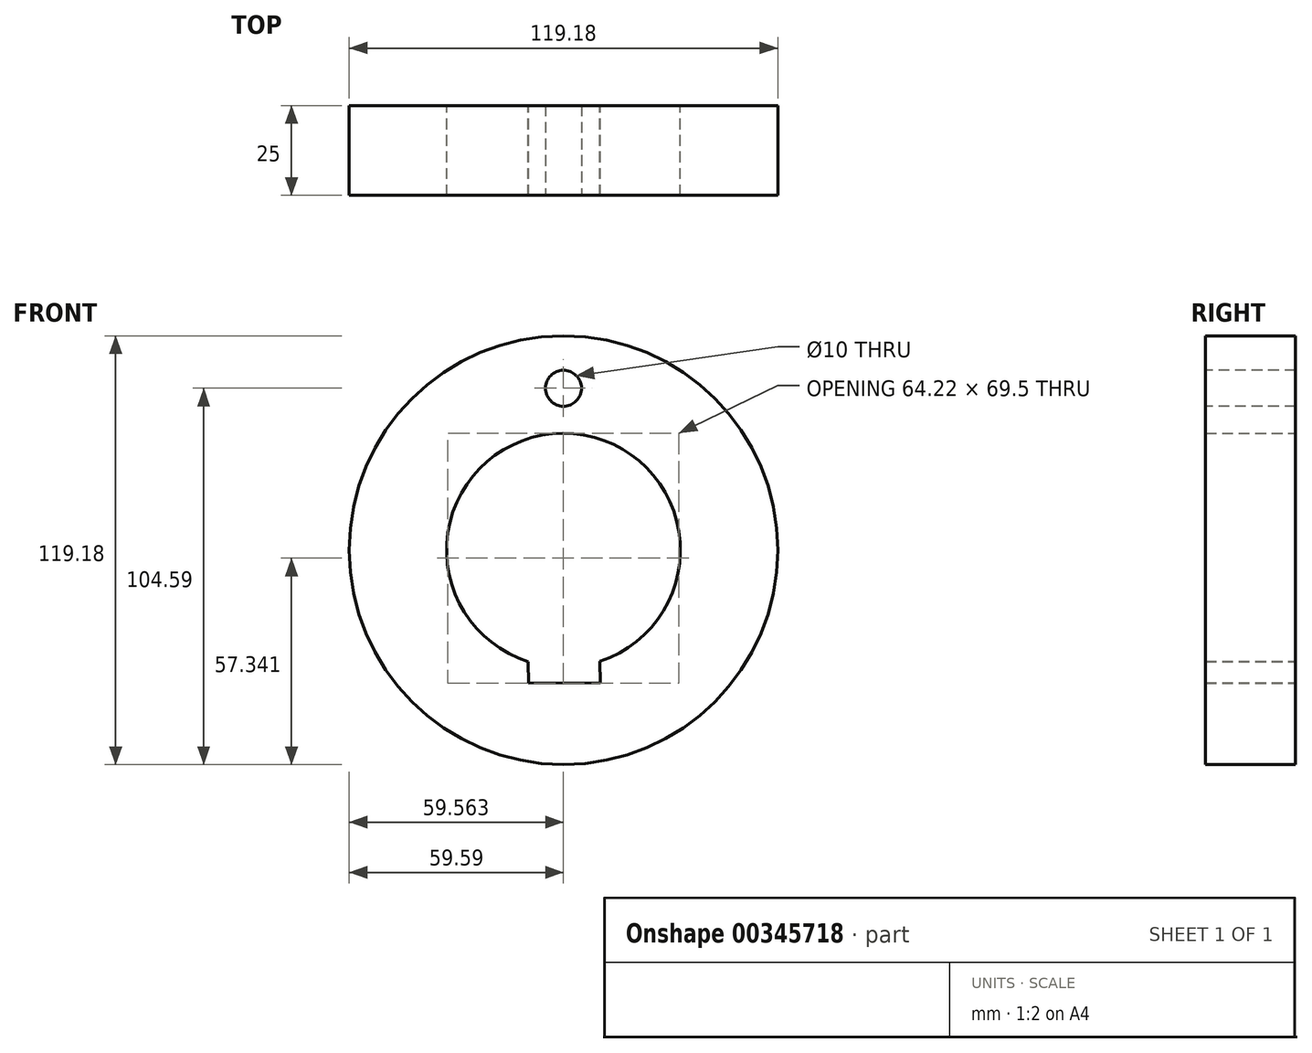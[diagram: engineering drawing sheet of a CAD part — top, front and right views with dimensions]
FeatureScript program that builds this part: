
annotation { "Feature Type Name" : "Feature", "Feature Type Description" : "" }
export const myFeature = defineFeature(function(context is Context, id is Id, definition is map)
    precondition{}
    {
        {
            var Q0;
            Q0=qCreatedBy(makeId("Front.planeOp"),FACE);
            var sketch = newSketch(context, id + "F0", { "sketchPlane" : qUnion([Q0])});
            skPoint(sketch, "E0.middle", {"position": v(0, -32.25) * mm});
            skLineSegment(sketch, "E1", {"start": v(-9.77, -31) * mm, "end": v(-9.73, -37) * mm});
            skLineSegment(sketch, "E2", {"start": v(-9.73, -37) * mm, "end": v(10.26, -36.89) * mm});
            skLineSegment(sketch, "E3", {"start": v(10.26, -36.89) * mm, "end": v(10.1, -30.9) * mm});
            skArc(sketch, "E4", {"start": v(10.1, -30.9) * mm, "mid": v(-0.17, 32.5) * mm, "end": v(-9.77, -31) * mm});
            skCircle(sketch, "E5", {"center": v(0, 0) * mm, "radius": 59.59 * mm});
            skCircle(sketch, "E6", {"center": v(0, 45) * mm, "radius": 5 * mm});
            skSolve(sketch);
        }
        {
            var Q0;
            Q0=makeQuery(id+"F0.imprint","IMPRINT",FACE,{"disambiguationData":[TD([[makeQuery(id+"F0.imprint","IMPRINT",EDGE,{"derivedFrom":sQuery(id+"F0.wireOp",EDGE,"E6")}),1.0]])]});
            var Q1;
            Q1=makeQuery(id+"F0.imprint","IMPRINT",FACE,{"disambiguationData":[TD([[makeQuery(id+"F0.imprint","IMPRINT",EDGE,{"derivedFrom":sQuery(id+"F0.wireOp",EDGE,"E1")}),-1.0]])]});
            extrude(context, id + "F1", {"entities" : qUnion([Q0, Q1]), "depth" : 25 * mm});
        }
        {
            var Q0;
            Q0=makeQuery(id+"F1.opExtrude","CAP_FACE",FACE,{"disambiguationData":[OSD([sQuery(id+"F0.wireOp",EDGE,"E1"),sQuery(id+"F0.wireOp",EDGE,"E2"),sQuery(id+"F0.wireOp",EDGE,"E3"),sQuery(id+"F0.wireOp",EDGE,"E4"),sQuery(id+"F0.wireOp",EDGE,"E5")])],"isStart":false});
            var sketch = newSketch(context, id + "F2", { "sketchPlane" : qUnion([Q0])});
            skCircle(sketch, "E7", {"center": v(0, 45) * mm, "radius": 5 * mm});
            skSolve(sketch);
        }
        {
            var Q0;
            Q0=sQuery(id+"F2.wireOp",VERTEX,"E7.center");
            var Q1;
            Q1=makeQuery(id+"F1.opExtrude","SWEPT_BODY",BODY,{"disambiguationData":[OSD([sQuery(id+"F0.wireOp",EDGE,"E1"),sQuery(id+"F0.wireOp",EDGE,"E2"),sQuery(id+"F0.wireOp",EDGE,"E3"),sQuery(id+"F0.wireOp",EDGE,"E4"),sQuery(id+"F0.wireOp",EDGE,"E5")])]});
            hole(context, id + "F3", {"style" : HoleStyle.SIMPLE, "endStyle" : HoleEndStyle.BLIND, "holeDiameter" : 10 * mm, "holeDepth" : 35 * mm, "isTappedThrough" : true, "tappedDepth" : 12 * mm, "tapClearance" : 3, "startFromSketch" : true, "locations" : qUnion([Q0]), "scope" : qUnion([Q1])});
        }
    });
